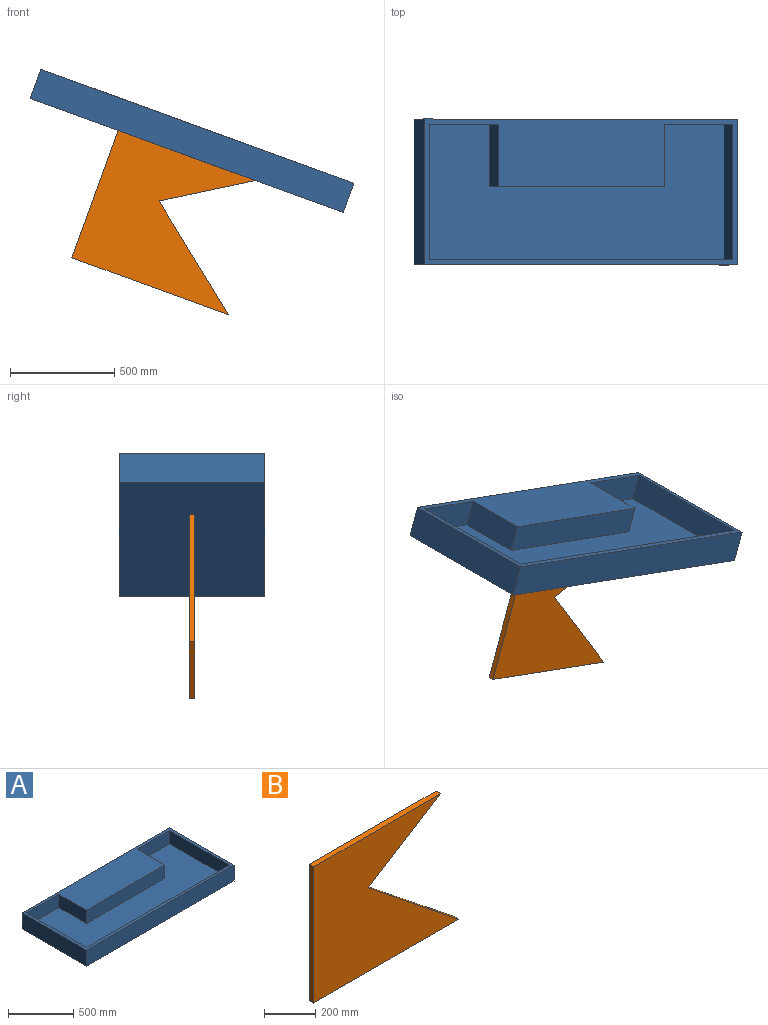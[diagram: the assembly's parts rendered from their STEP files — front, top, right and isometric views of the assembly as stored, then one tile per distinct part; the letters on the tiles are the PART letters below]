
ASSEMBLY  parts=2 mates=1
PART A: 15 faces, bbox 1600x700x150 mm
  f0: plane 1600x700mm, normal (0,0,1), area 369499.4mm2, adj f1,f2,f3,f4,f6,f7,f8,f9
  f1: plane 1600x150mm, normal (0,1,0), area 240000mm2, adj f0,f2,f4,f5
  f2: plane 700x150mm, normal (-1,0,0), area 105000mm2, adj f0,f1,f3,f5
  f3: plane 1600x150mm, normal (0,-1,0), area 240000mm2, adj f0,f2,f4,f5
  f4: plane 700x150mm, normal (1,0,0), area 105000mm2, adj f0,f1,f3,f5
  f5: plane 1600x700mm, normal (0,0,-1), area 1120000mm2, adj f1,f2,f3,f4
  f6: plane 349.2x124.6mm, normal (0,-1,0), area 43510.3mm2, adj f0,f7,f13,f14
  f7: plane 300x124.6mm, normal (1,0,0), area 37380mm2, adj f0,f6,f8,f14
  f8: plane 850.8x124.6mm, normal (0,-1,0), area 106009.7mm2, adj f0,f7,f9,f14
  f9: plane 300x124.6mm, normal (-1,0,0), area 37380mm2, adj f0,f8,f10,f14
  f10: plane 349.2x124.6mm, normal (0,-1,0), area 43510.3mm2, adj f0,f9,f11,f14
  f11: plane 649.2x124.6mm, normal (1,0,0), area 80890.3mm2, adj f0,f10,f12,f14
  f12: plane 1549.2x124.6mm, normal (0,1,0), area 193030.3mm2, adj f0,f11,f13,f14
  f13: plane 649.2x124.6mm, normal (-1,0,0), area 80890.3mm2, adj f0,f6,f12,f14
  f14: plane 1549.2x649.2mm, normal (0,0,1), area 750500.6mm2, adj f6,f7,f8,f9,f10,f11,f12,f13
PART B: 7 faces, bbox 800x25.4x650 mm
  f0: plane 650x25.4mm, normal (-1,0,0), area 16510mm2, adj f1,f4,f5,f6
  f1: plane 800x25.4mm, normal (0,0,-1), area 20320mm2, adj f0,f2,f5,f6
  f2: plane 500x400mm, normal (0.62,0,0.78), area 16263.9mm2, adj f1,f3,f5,f6
  f3: plane 400x250mm, normal (0.53,0,-0.85), area 11981.2mm2, adj f2,f4,f5,f6
  f4: plane 700x25.4mm, normal (0,0,1), area 17780mm2, adj f0,f3,f5,f6
  f5: plane 800x650mm, normal (0,-1,0), area 345000mm2, adj f0,f1,f2,f3,f4
  f6: plane 800x650mm, normal (0,1,0), area 345000mm2, adj f0,f1,f2,f3,f4
PLACE A rot(axis=(0,1,0),20deg) t=(-264.66,-468.68,354.72)mm
PLACE B rot(axis=(0,1,0),20deg) t=(-64.11,-105.98,-409.99)mm
MATE fastened A.f5 <-> B.f4  axis (-0.34,0,-0.94) through (487.09,-118.68,81.1)mm
